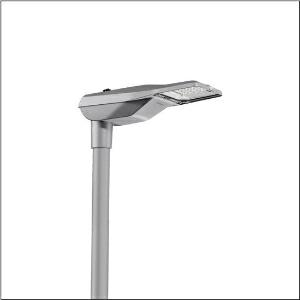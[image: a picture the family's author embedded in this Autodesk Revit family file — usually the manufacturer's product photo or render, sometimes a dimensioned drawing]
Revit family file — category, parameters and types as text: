
# Revit family: streetlight_sl_21_micro___st1_0a_5xe1d43s08db_64f0
name_source: partatom
category: Lighting Fixtures
units: mm (PartAtom-declared; Revit-internal decimal feet)

## family parameters
Cut with Voids When Loaded = No
Host = Face
Light Source = No
Part Type = Normal
Room Calculation Point = No
Round Connector Dimension = Use Diameter
Shared = No

## types (1)
- --- (1 x LED, 5320 lm, 39.1 W, 4000K)
    Apparent Load = 39 VA
    CIE Flux Codes = 37 72 97 100 100
    Color Rendering = 70
    Color Temperature = 4000K
    Default Elevation = 1800 mm
    Description = Streetlight SL 21 micro, mast luminaire, primary light control with lens, of PMMA, primary optical cover: cover, of toughened safety glass, transparent, light distribution: ST1.0a, light emission: direct distribution, primary light characteristic: asymmetric, installation type: side-entry, post-top, LED, High Power LED, rated luminous flux: 5.320lm, luminous efficacy: 136lm/W, light colour: 740, colour temperature: 4000K, control: flexible luminous flux parameterisation, time-dependent luminous flux control, constant luminous flux control, overheat protection, presetting dimming logarithmic, mains connection: 220..240V, AC, 50/60Hz, start of lifetime: 39W, end of service life: 41W, reduction: 18W, luminaire housing, of diecast aluminium, powder-coated, Siteco® metallic grey (DB 702S), corrosivity category C5 mid according to DIN EN ISO 12944, please order mast flange separately, inclination adjustable: 0°, 5°, 10°, 15°, sealing non-destructively replaceable, multi-level sealing system, length: 528mm, width: 235mm, height: 110mm, mast flange for spigot size: 42mm (side-entry): 5XC10008XM4, 60/48mm (side-entry/post-top): 5XC10108XM2, 76/60mm (side-entry/post-top): 5XC10108XM1, Smart Interface above, protection rating (complete): IP66, insulation class (complete): insulation class II (safety insulation), certification: CE, ENEC, ENEC+, VDE, impact resistance: IK09, permissible operating ambient temperature for outdoor applications: -40..+50°C, standard-compliant lighting for roads and squares, packaging unit: 1 piece

Light Distribution: ST1.0a
    Height = 110 mm
    Lamp = 1 x LED
    Lamp Light Flux = 5320 lm
    Lamp Power = 39.1 W
    Lamp count = 1
    Length = 528 mm
    Luminous efficacy = 136 lm/W
    Manufacturer = Siteco
    ModVariant = No
    Model = 5XE1D43S08DB
    Number of Poles = 1
    OnlyDefault = Yes
    Power Factor = 1
    Product Name = Streetlight SL 21 micro | ST1.0a
    Product group = mast luminaire | pylon top
    ProductGroupID = 6100
    Protection Class = Protection class II
    Protection Degree = IP 66
    RLX_Detail_Level = 1
    RLX_Emergency_Light_Flux = 0 lm
    RLX_Emergency_Type = 0
    RLX_Emergency_Type_DB = No
    RlxData = <blob elided: 98529 chars, md5=1f5fe75a>
    Socket = socket
    Standby Power = 0 W
    System Light Flux = 5320 lm
    System Power = 39 W
    Type Comments = factory setting: luminous flux: 100 % | dim-lin: 254 | 765 mA
    Type Image = l_1277292.jpg
    URL = http://relux.com
    VarID = @adj_105953
    Voltage = 0 V
    Weight = 0.00 kg
    Width = 235 mm

## geometry (parser evidence)
native form markers: Blend x4, Sweep x10
no freeform markers — native parametric forms only
